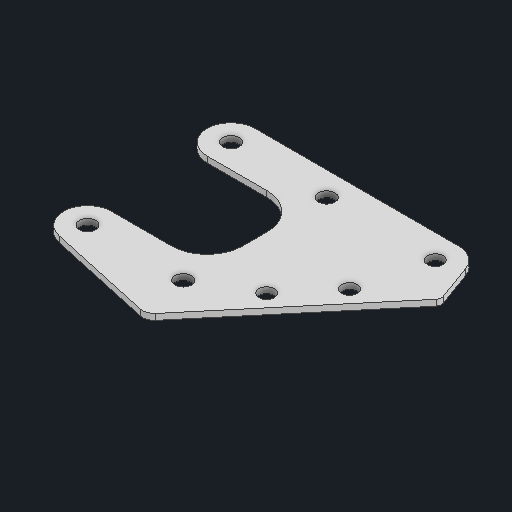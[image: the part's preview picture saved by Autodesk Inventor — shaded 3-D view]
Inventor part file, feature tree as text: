
AUTODESK INVENTOR PART (.ipt)
format: ipt  version: 2025 (Build 290162000, 162)  size: 136,704 bytes
history: native  units: in
note: dims shown in document units (in); Inventor stores cm internally (conversion verified against a paired STEP export)
features: other x3, extrude x1, sketch x1
ambient origin geometry x8: Origin, YZ Plane, XZ Plane, XY Plane, X Axis, Y Axis, Z Axis, Center Point
bodies: Solid1 (feature_tree)
feature tree (5):
  other  "Blocks"
  extrude  "Extrusion1"  Depth=0.125in
  sketch  "Sketch1"  dims[d0=0.164in d1=0.5in d6=0.375in d8=0.164in d9=0.0625in d10=0.0625in d11=0.0in d14=0.164in d15=0.615in d17=0.125in]
  other  "main"
  other  "main:1"
